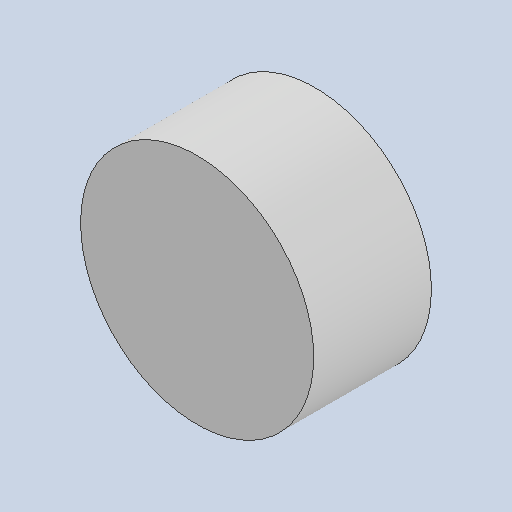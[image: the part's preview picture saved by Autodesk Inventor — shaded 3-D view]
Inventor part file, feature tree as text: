
AUTODESK INVENTOR PART (.ipt)
format: ipt  version: 2022 (Build 260153070, 153G)  size: 87,552 bytes
history: native  units: in
note: dims shown in document units (in); Inventor stores cm internally (conversion verified against a paired STEP export)
features: other x3, sketch x1, plane x1
ambient origin geometry x8: Origin, YZ Plane, XZ Plane, XY Plane, X Axis, Y Axis, Z Axis, Center Point
bodies: Solid1 (feature_tree)
feature tree (5):
  other  "TTencoderspacer.ipt"
  other  "Solid1::TTencoderspacer.ipt"
  other  "TaggingFeature1"
  sketch  "Sketch1"  dims[d0=0.3937in]
  plane  "Work Plane1"
